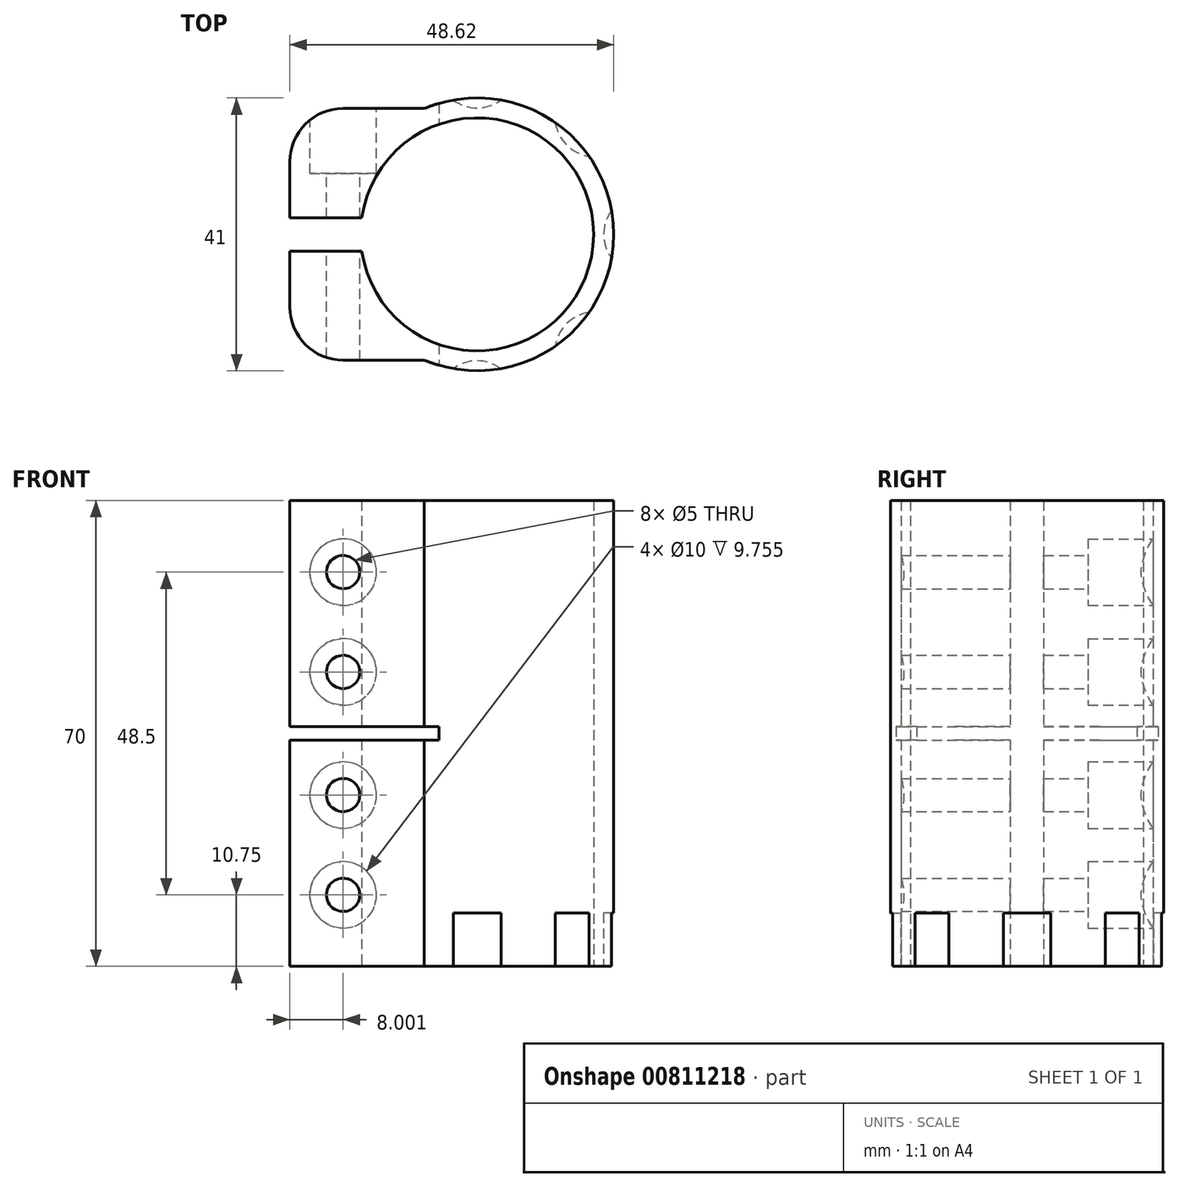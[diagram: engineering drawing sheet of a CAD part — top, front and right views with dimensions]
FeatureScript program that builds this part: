
annotation { "Feature Type Name" : "Feature", "Feature Type Description" : "" }
export const myFeature = defineFeature(function(context is Context, id is Id, definition is map)
    precondition{}
    {
        {
            var Q0;
            Q0=qCreatedBy(makeId("Top.planeOp"),FACE);
            var sketch = newSketch(context, id + "F0", { "sketchPlane" : qUnion([Q0])});
            skArc(sketch, "E0", {"start": v(-17.32, -2.5) * mm, "mid": v(17.5, 0) * mm, "end": v(-17.32, 2.5) * mm});
            skArc(sketch, "E1", {"start": v(-7.92, -18.9) * mm, "mid": v(20.5, 0) * mm, "end": v(-7.92, 18.9) * mm});
            skLineSegment(sketch, "E2", {"start": v(-17.32, 2.5) * mm, "end": v(-28.12, 2.5) * mm});
            skLineSegment(sketch, "E3", {"start": v(-28.12, 2.5) * mm, "end": v(-28.12, 10.9) * mm});
            skLineSegment(sketch, "E4", {"start": v(-20.12, 18.9) * mm, "end": v(-7.92, 18.9) * mm});
            skPoint(sketch, "E5.visualSharp", {"position": v(-28.12, 18.9) * mm});
            skArc(sketch, "E5.filletArc", {"start": v(-20.12, 18.9) * mm, "mid": v(-25.78, 16.57) * mm, "end": v(-28.12, 10.9) * mm});
            skLineSegment(sketch, "E6", {"start": v(0, 0) * mm, "end": v(33.6, 0) * mm});
            skLineSegment(sketch, "E7.MirrorCS", {"start": v(-20.12, -18.9) * mm, "end": v(-7.92, -18.9) * mm});
            skArc(sketch, "E8.MirrorCS", {"start": v(-20.12, -18.9) * mm, "mid": v(-25.78, -16.57) * mm, "end": v(-28.12, -10.9) * mm});
            skLineSegment(sketch, "E9.MirrorCS", {"start": v(-28.12, -2.5) * mm, "end": v(-28.12, -10.9) * mm});
            skLineSegment(sketch, "E10.MirrorCS", {"start": v(-17.32, -2.5) * mm, "end": v(-28.12, -2.5) * mm});
            skSolve(sketch);
        }
        {
            var Q0;
            {var subQ0=sQuery(id+"F0.wireOp",EDGE,"E2");Q0=makeQuery(id+"F0.imprint","IMPRINT",FACE,{"disambiguationData":[TD([[makeQuery(id+"F0.imprint","IMPRINT",EDGE,{"derivedFrom":subQ0}),-1.0]])]});}
            var Q1;
            {var subQ0=sQuery(id+"F0.wireOp",EDGE,"E7.MirrorCS");Q1=makeQuery(id+"F0.imprint","IMPRINT",FACE,{"disambiguationData":[TD([[makeQuery(id+"F0.imprint","IMPRINT",EDGE,{"derivedFrom":subQ0}),1.0]])]});}
            extrude(context, id + "F1", {"entities" : qUnion([Q0, Q1]), "endBound" : BoundingType.SYMMETRIC, "depth" : 70 * mm, "offsetDistance" : 25 * mm});
        }
        {
            var Q0;
            Q0=makeQuery(id+"F1.opExtrude","SWEPT_FACE",FACE,{"disambiguationData":[OSD([sQuery(id+"F0.wireOp",EDGE,"E4")])]});
            var sketch = newSketch(context, id + "F2", { "sketchPlane" : qUnion([Q0])});
            skPoint(sketch, "E11", {"position": v(20.12, -24.25) * mm});
            skPoint(sketch, "E12", {"position": v(20.12, -9.25) * mm});
            skPoint(sketch, "E13", {"position": v(20.12, 9.25) * mm});
            skPoint(sketch, "E14", {"position": v(20.12, 24.25) * mm});
            skSolve(sketch);
        }
        {
            var Q0;
            Q0=sQuery(id+"F2.wireOp",VERTEX,"E11");
            var Q1;
            Q1=sQuery(id+"F2.wireOp",VERTEX,"E12");
            var Q2;
            Q2=sQuery(id+"F2.wireOp",VERTEX,"E13");
            var Q3;
            Q3=sQuery(id+"F2.wireOp",VERTEX,"E14");
            var Q4;
            Q4=makeQuery(id+"F1.opExtrude","SWEPT_BODY",BODY,{"disambiguationData":[OSD([sQuery(id+"F0.wireOp",EDGE,"E0"),sQuery(id+"F0.wireOp",EDGE,"E1"),sQuery(id+"F0.wireOp",EDGE,"E2"),sQuery(id+"F0.wireOp",EDGE,"E3"),sQuery(id+"F0.wireOp",EDGE,"E4"),sQuery(id+"F0.wireOp",EDGE,"E5.filletArc"),sQuery(id+"F0.wireOp",EDGE,"E7.MirrorCS"),sQuery(id+"F0.wireOp",EDGE,"E8.MirrorCS"),sQuery(id+"F0.wireOp",EDGE,"E9.MirrorCS"),sQuery(id+"F0.wireOp",EDGE,"E10.MirrorCS")])]});
            hole(context, id + "F3", {"style" : HoleStyle.C_BORE, "endStyle" : HoleEndStyle.THROUGH, "holeDiameter" : 5 * mm, "cBoreDiameter" : 10 * mm, "cBoreDepth" : 8 * mm, "majorDiameter" : 5 * mm, "isTappedThrough" : true, "tappedDepth" : 12 * mm, "tapClearance" : 3, "locations" : qUnion([Q0, Q1, Q2, Q3]), "scope" : qUnion([Q4])});
        }
        {
            var Q0;
            Q0=qCreatedBy(makeId("Front.planeOp"),FACE);
            var sketch = newSketch(context, id + "F4", { "sketchPlane" : qUnion([Q0])});
            skLineSegment(sketch, "E15.bottom", {"start": v(-28.12, -1) * mm, "end": v(-5.72, -1) * mm});
            skLineSegment(sketch, "E15.top", {"start": v(-28.12, 1) * mm, "end": v(-5.72, 1) * mm});
            skLineSegment(sketch, "E15.left", {"start": v(-28.12, -1) * mm, "end": v(-28.12, 1) * mm});
            skLineSegment(sketch, "E15.right", {"start": v(-5.72, -1) * mm, "end": v(-5.72, 1) * mm});
            skSolve(sketch);
        }
        {
            var Q0;
            Q0=makeQuery(id+"F4.imprint","IMPRINT",FACE,{"disambiguationData":[TD([[makeQuery(id+"F4.imprint","IMPRINT",EDGE,{"derivedFrom":sQuery(id+"F4.wireOp",EDGE,"E15.bottom")}),1.0]])]});
            extrude(context, id + "F5", {"entities" : qUnion([Q0]), "operationType" : NewBodyOperationType.REMOVE, "endBound" : BoundingType.SYMMETRIC, "oppositeDirection" : true, "depth" : 50 * mm, "offsetDistance" : 25 * mm});
        }
        {
            var Q0;
            Q0=makeQuery(id+"F1.opExtrude","CAP_FACE",FACE,{"disambiguationData":[OSD([sQuery(id+"F0.wireOp",EDGE,"E0"),sQuery(id+"F0.wireOp",EDGE,"E1"),sQuery(id+"F0.wireOp",EDGE,"E2"),sQuery(id+"F0.wireOp",EDGE,"E3"),sQuery(id+"F0.wireOp",EDGE,"E4"),sQuery(id+"F0.wireOp",EDGE,"E5.filletArc"),sQuery(id+"F0.wireOp",EDGE,"E7.MirrorCS"),sQuery(id+"F0.wireOp",EDGE,"E8.MirrorCS"),sQuery(id+"F0.wireOp",EDGE,"E9.MirrorCS"),sQuery(id+"F0.wireOp",EDGE,"E10.MirrorCS")])],"isStart":true});
            var sketch = newSketch(context, id + "F6", { "sketchPlane" : qUnion([Q0])});
            skCircle(sketch, "E16", {"center": v(0, -25) * mm, "radius": 6 * mm});
            skCircle(sketch, "E17.1.0", {"center": v(17.68, -17.68) * mm, "radius": 6 * mm});
            skCircle(sketch, "E17.2.0", {"center": v(25, 0) * mm, "radius": 6 * mm});
            skCircle(sketch, "E17.3.0", {"center": v(17.68, 17.68) * mm, "radius": 6 * mm});
            skCircle(sketch, "E17.4.0", {"center": v(0, 25) * mm, "radius": 6 * mm});
            skPoint(sketch, "E17.center", {"position": v(0, 0) * mm});
            skLineSegment(sketch, "E17.anchor1", {"start": v(0, 0) * mm, "end": v(0, -25) * mm, "construction": true});
            skLineSegment(sketch, "E17.anchor2", {"start": v(0, 0) * mm, "end": v(0, 25) * mm, "construction": true});
            skSolve(sketch);
        }
        {
            var Q0;
            {var subQ0=sQuery(id+"F6.wireOp",EDGE,"E17.4.0");var subQ1=makeQuery(id+"F1.opExtrude","CAP_EDGE",EDGE,{"disambiguationData":[OSD([sQuery(id+"F0.wireOp",EDGE,"E1")])],"isStart":true});var subQ2=makeQuery(id+"F6.imprint","INTERSECT",VERTEX,{"disambiguationData":[OD(0.0)],"derivedFrom":[subQ1,subQ0]});Q0=makeQuery(id+"F6.imprint","IMPRINT",FACE,{"disambiguationData":[TD([[makeQuery(id+"F6.imprint","IMPRINT",EDGE,{"disambiguationData":[TD([[subQ2,1.0]])],"derivedFrom":subQ0}),1.0]])]});}
            var Q1;
            {var subQ0=sQuery(id+"F6.wireOp",EDGE,"E17.3.0");var subQ1=makeQuery(id+"F1.opExtrude","CAP_EDGE",EDGE,{"disambiguationData":[OSD([sQuery(id+"F0.wireOp",EDGE,"E1")])],"isStart":true});var subQ2=makeQuery(id+"F6.imprint","INTERSECT",VERTEX,{"disambiguationData":[OD(0.0)],"derivedFrom":[subQ1,subQ0]});Q1=makeQuery(id+"F6.imprint","IMPRINT",FACE,{"disambiguationData":[TD([[makeQuery(id+"F6.imprint","IMPRINT",EDGE,{"disambiguationData":[TD([[subQ2,1.0]])],"derivedFrom":subQ0}),1.0]])]});}
            var Q2;
            {var subQ0=sQuery(id+"F6.wireOp",EDGE,"E17.2.0");var subQ1=makeQuery(id+"F1.opExtrude","CAP_EDGE",EDGE,{"disambiguationData":[OSD([sQuery(id+"F0.wireOp",EDGE,"E1")])],"isStart":true});var subQ2=makeQuery(id+"F6.imprint","INTERSECT",VERTEX,{"disambiguationData":[OD(0.0)],"derivedFrom":[subQ1,subQ0]});Q2=makeQuery(id+"F6.imprint","IMPRINT",FACE,{"disambiguationData":[TD([[makeQuery(id+"F6.imprint","IMPRINT",EDGE,{"disambiguationData":[TD([[subQ2,-1.0]])],"derivedFrom":subQ0}),1.0]])]});}
            var Q3;
            {var subQ0=sQuery(id+"F6.wireOp",EDGE,"E17.1.0");var subQ1=makeQuery(id+"F1.opExtrude","CAP_EDGE",EDGE,{"disambiguationData":[OSD([sQuery(id+"F0.wireOp",EDGE,"E1")])],"isStart":true});var subQ2=makeQuery(id+"F6.imprint","INTERSECT",VERTEX,{"disambiguationData":[OD(0.0)],"derivedFrom":[subQ1,subQ0]});Q3=makeQuery(id+"F6.imprint","IMPRINT",FACE,{"disambiguationData":[TD([[makeQuery(id+"F6.imprint","IMPRINT",EDGE,{"disambiguationData":[TD([[subQ2,-1.0]])],"derivedFrom":subQ0}),1.0]])]});}
            var Q4;
            {var subQ0=sQuery(id+"F6.wireOp",EDGE,"E16");var subQ1=makeQuery(id+"F1.opExtrude","CAP_EDGE",EDGE,{"disambiguationData":[OSD([sQuery(id+"F0.wireOp",EDGE,"E1")])],"isStart":true});var subQ2=makeQuery(id+"F6.imprint","INTERSECT",VERTEX,{"disambiguationData":[OD(0.0)],"derivedFrom":[subQ1,subQ0]});Q4=makeQuery(id+"F6.imprint","IMPRINT",FACE,{"disambiguationData":[TD([[makeQuery(id+"F6.imprint","IMPRINT",EDGE,{"disambiguationData":[TD([[subQ2,-1.0]])],"derivedFrom":subQ0}),1.0]])]});}
            var Q5;
            {var subQ0=sQuery(id+"F6.wireOp",EDGE,"E17.4.0");var subQ1=makeQuery(id+"F1.opExtrude","CAP_EDGE",EDGE,{"disambiguationData":[OSD([sQuery(id+"F0.wireOp",EDGE,"E1")])],"isStart":true});var subQ2=makeQuery(id+"F6.imprint","INTERSECT",VERTEX,{"disambiguationData":[OD(0.0)],"derivedFrom":[subQ1,subQ0]});Q5=makeQuery(id+"F6.imprint","IMPRINT",FACE,{"disambiguationData":[TD([[makeQuery(id+"F6.imprint","IMPRINT",EDGE,{"disambiguationData":[TD([[subQ2,-1.0]])],"derivedFrom":subQ0}),1.0]])]});}
            var Q6;
            {var subQ0=sQuery(id+"F6.wireOp",EDGE,"E17.3.0");var subQ1=makeQuery(id+"F1.opExtrude","CAP_EDGE",EDGE,{"disambiguationData":[OSD([sQuery(id+"F0.wireOp",EDGE,"E1")])],"isStart":true});var subQ2=makeQuery(id+"F6.imprint","INTERSECT",VERTEX,{"disambiguationData":[OD(0.0)],"derivedFrom":[subQ1,subQ0]});Q6=makeQuery(id+"F6.imprint","IMPRINT",FACE,{"disambiguationData":[TD([[makeQuery(id+"F6.imprint","IMPRINT",EDGE,{"disambiguationData":[TD([[subQ2,-1.0]])],"derivedFrom":subQ0}),1.0]])]});}
            var Q7;
            {var subQ0=sQuery(id+"F6.wireOp",EDGE,"E17.2.0");var subQ1=makeQuery(id+"F1.opExtrude","CAP_EDGE",EDGE,{"disambiguationData":[OSD([sQuery(id+"F0.wireOp",EDGE,"E1")])],"isStart":true});var subQ2=makeQuery(id+"F6.imprint","INTERSECT",VERTEX,{"disambiguationData":[OD(0.0)],"derivedFrom":[subQ1,subQ0]});Q7=makeQuery(id+"F6.imprint","IMPRINT",FACE,{"disambiguationData":[TD([[makeQuery(id+"F6.imprint","IMPRINT",EDGE,{"disambiguationData":[TD([[subQ2,1.0]])],"derivedFrom":subQ0}),1.0]])]});}
            var Q8;
            {var subQ0=sQuery(id+"F6.wireOp",EDGE,"E17.1.0");var subQ1=makeQuery(id+"F1.opExtrude","CAP_EDGE",EDGE,{"disambiguationData":[OSD([sQuery(id+"F0.wireOp",EDGE,"E1")])],"isStart":true});var subQ2=makeQuery(id+"F6.imprint","INTERSECT",VERTEX,{"disambiguationData":[OD(0.0)],"derivedFrom":[subQ1,subQ0]});Q8=makeQuery(id+"F6.imprint","IMPRINT",FACE,{"disambiguationData":[TD([[makeQuery(id+"F6.imprint","IMPRINT",EDGE,{"disambiguationData":[TD([[subQ2,1.0]])],"derivedFrom":subQ0}),1.0]])]});}
            var Q9;
            {var subQ0=sQuery(id+"F6.wireOp",EDGE,"E16");var subQ1=makeQuery(id+"F1.opExtrude","CAP_EDGE",EDGE,{"disambiguationData":[OSD([sQuery(id+"F0.wireOp",EDGE,"E1")])],"isStart":true});var subQ2=makeQuery(id+"F6.imprint","INTERSECT",VERTEX,{"disambiguationData":[OD(0.0)],"derivedFrom":[subQ1,subQ0]});Q9=makeQuery(id+"F6.imprint","IMPRINT",FACE,{"disambiguationData":[TD([[makeQuery(id+"F6.imprint","IMPRINT",EDGE,{"disambiguationData":[TD([[subQ2,1.0]])],"derivedFrom":subQ0}),1.0]])]});}
            extrude(context, id + "F7", {"entities" : qUnion([Q0, Q1, Q2, Q3, Q4, Q5, Q6, Q7, Q8, Q9]), "operationType" : NewBodyOperationType.REMOVE, "oppositeDirection" : true, "depth" : 8 * mm, "offsetDistance" : 25 * mm});
        }
    });
